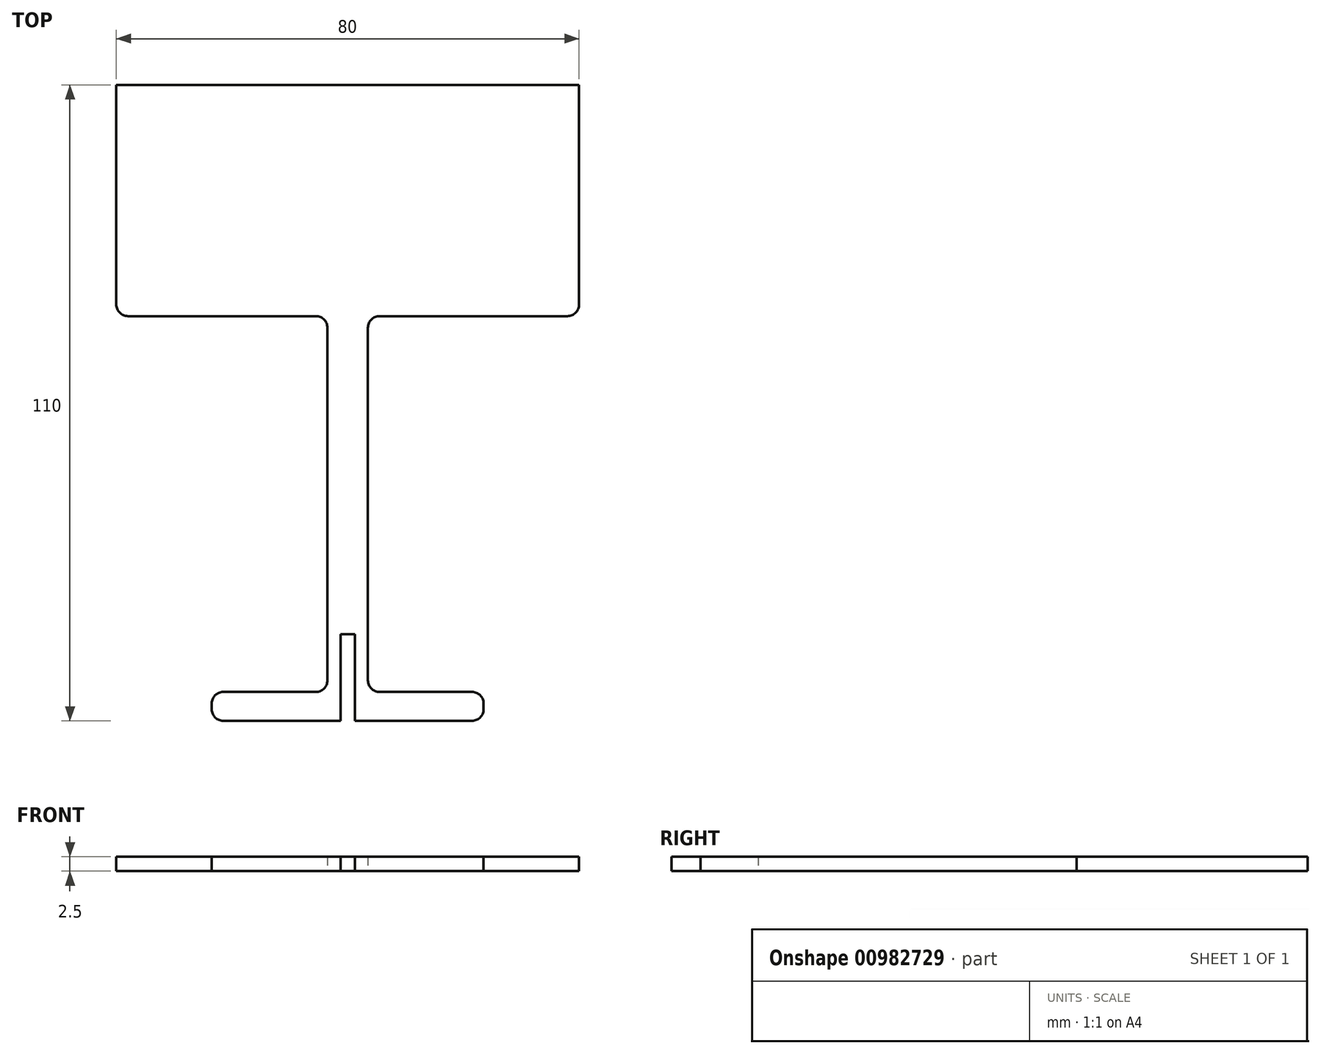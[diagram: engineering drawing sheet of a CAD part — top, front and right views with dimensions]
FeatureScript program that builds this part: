
annotation { "Feature Type Name" : "Feature", "Feature Type Description" : "" }
export const myFeature = defineFeature(function(context is Context, id is Id, definition is map)
    precondition{}
    {
        {
            var Q0;
            Q0=qCreatedBy(makeId("Top.planeOp"),FACE);
            var sketch = newSketch(context, id + "F0", { "sketchPlane" : qUnion([Q0])});
            skLineSegment(sketch, "E0", {"start": v(-40, 0) * mm, "end": v(40, 0) * mm});
            skPoint(sketch, "E1", {"position": v(0, 0) * mm});
            skLineSegment(sketch, "E2", {"start": v(-3.5, 0) * mm, "end": v(-3.5, -65) * mm});
            skLineSegment(sketch, "E3", {"start": v(-3.5, -65) * mm, "end": v(-23.5, -65) * mm});
            skLineSegment(sketch, "E4", {"start": v(-23.5, -65) * mm, "end": v(-23.5, -70) * mm});
            skLineSegment(sketch, "E5", {"start": v(-23.5, -70) * mm, "end": v(23.5, -70) * mm});
            skLineSegment(sketch, "E6", {"start": v(23.5, -70) * mm, "end": v(23.5, -65) * mm});
            skLineSegment(sketch, "E7", {"start": v(23.5, -65) * mm, "end": v(3.5, -65) * mm});
            skLineSegment(sketch, "E8", {"start": v(3.5, -65) * mm, "end": v(3.5, 0) * mm});
            skLineSegment(sketch, "E9.bottom", {"start": v(1.25, -70) * mm, "end": v(-1.25, -70) * mm});
            skLineSegment(sketch, "E9.top", {"start": v(1.25, -55) * mm, "end": v(-1.25, -55) * mm});
            skLineSegment(sketch, "E9.left", {"start": v(1.25, -70) * mm, "end": v(1.25, -55) * mm});
            skLineSegment(sketch, "E9.right", {"start": v(-1.25, -70) * mm, "end": v(-1.25, -55) * mm});
            skPoint(sketch, "E9.middle", {"position": v(0, -62.5) * mm});
            skLineSegment(sketch, "E10.bottom", {"start": v(-23.5, -70) * mm, "end": v(-17.5, -70) * mm});
            skLineSegment(sketch, "E10.top", {"start": v(-23.5, -70.3) * mm, "end": v(-17.5, -70.3) * mm});
            skLineSegment(sketch, "E10.left", {"start": v(-23.5, -70) * mm, "end": v(-23.5, -70.3) * mm});
            skLineSegment(sketch, "E10.right", {"start": v(-17.5, -70) * mm, "end": v(-17.5, -70.3) * mm});
            skLineSegment(sketch, "E11.MirrorCS", {"start": v(23.5, -70) * mm, "end": v(17.5, -70) * mm});
            skLineSegment(sketch, "E12.MirrorCS", {"start": v(17.5, -70) * mm, "end": v(17.5, -70.3) * mm});
            skLineSegment(sketch, "E13.MirrorCS", {"start": v(23.5, -70.3) * mm, "end": v(17.5, -70.3) * mm});
            skLineSegment(sketch, "E14.MirrorCS", {"start": v(23.5, -70) * mm, "end": v(23.5, -70.3) * mm});
            skLineSegment(sketch, "E15", {"start": v(-40, 0) * mm, "end": v(-40, 40) * mm});
            skLineSegment(sketch, "E16", {"start": v(-40, 40) * mm, "end": v(40, 40) * mm});
            skLineSegment(sketch, "E17", {"start": v(40, 40) * mm, "end": v(40, 0) * mm});
            skSolve(sketch);
        }
        {
            var Q0;
            {var subQ0=sQuery(id+"F0.wireOp",EDGE,"im0v1Rov-prSM-cwdN-f0IW-ScqFdnQkXUSi");Q0=makeQuery(id+"F0.imprint","IMPRINT",FACE,{"disambiguationData":[TD([[makeQuery(id+"F0.imprint","IMPRINT",EDGE,{"derivedFrom":subQ0}),1.0]])]});}
            var Q1;
            {var subQ7=sQuery(id+"F0.wireOp",EDGE,"E2");Q1=makeQuery(id+"F0.imprint","IMPRINT",FACE,{"disambiguationData":[TD([[makeQuery(id+"F0.imprint","IMPRINT",EDGE,{"derivedFrom":subQ7}),1.0]])]});}
            var Q2;
            Q2=makeQuery(id+"F0.imprint","IMPRINT",FACE,{"disambiguationData":[TD([[makeQuery(id+"F0.imprint","IMPRINT",EDGE,{"derivedFrom":sQuery(id+"F0.wireOp",EDGE,"E10.bottom")}),-1.0]])]});
            var Q3;
            Q3=makeQuery(id+"F0.imprint","IMPRINT",FACE,{"disambiguationData":[TD([[makeQuery(id+"F0.imprint","IMPRINT",EDGE,{"derivedFrom":sQuery(id+"F0.wireOp",EDGE,"E11.MirrorCS")}),1.0]])]});
            var Q4;
            {var subQ0=sQuery(id+"F0.wireOp",EDGE,"E15");Q4=makeQuery(id+"F0.imprint","IMPRINT",FACE,{"disambiguationData":[TD([[makeQuery(id+"F0.imprint","IMPRINT",EDGE,{"derivedFrom":subQ0}),-1.0]])]});}
            extrude(context, id + "F1", {"entities" : qUnion([Q0, Q1, Q2, Q3, Q4]), "flatOperationType" : FlatOperationType.REMOVE, "depth" : 2.5 * mm, "offsetDistance" : 25 * mm, "domain" : OperationDomain.MODEL});
        }
        {
            var Q0;
            Q0=makeQuery(id+"F1.opExtrude","SWEPT_EDGE",EDGE,{"disambiguationData":[OSD([sQuery(id+"F0.wireOp",EDGE,"E0"),sQuery(id+"F0.wireOp",EDGE,"E2")])]});
            var Q1;
            Q1=makeQuery(id+"F1.opExtrude","SWEPT_EDGE",EDGE,{"disambiguationData":[OSD([sQuery(id+"F0.wireOp",EDGE,"E0"),sQuery(id+"F0.wireOp",EDGE,"E8")])]});
            var Q2;
            Q2=makeQuery(id+"F1.opExtrude","SWEPT_EDGE",EDGE,{"disambiguationData":[OSD([sQuery(id+"F0.wireOp",EDGE,"E0"),sQuery(id+"F0.wireOp",EDGE,"im0v1Rov-prSM-cwdN-f0IW-ScqFdnQkXUSi")])]});
            var Q3;
            Q3=makeQuery(id+"F1.opExtrude","SWEPT_EDGE",EDGE,{"disambiguationData":[OSD([sQuery(id+"F0.wireOp",EDGE,"E0"),sQuery(id+"F0.wireOp",EDGE,"IfBi3EXo-PReU-dRJG-joro-0UU4bWJMkuGZ")])]});
            var Q4;
            Q4=makeQuery(id+"F1.opExtrude","SWEPT_EDGE",EDGE,{"disambiguationData":[OSD([sQuery(id+"F0.wireOp",EDGE,"im0v1Rov-prSM-cwdN-f0IW-ScqFdnQkXUSi"),sQuery(id+"F0.wireOp",EDGE,"IfBi3EXo-PReU-dRJG-joro-0UU4bWJMkuGZ")])]});
            var Q5;
            Q5=makeQuery(id+"F1.opExtrude","SWEPT_EDGE",EDGE,{"disambiguationData":[OSD([sQuery(id+"F0.wireOp",EDGE,"E7"),sQuery(id+"F0.wireOp",EDGE,"E8")])]});
            var Q6;
            Q6=makeQuery(id+"F1.opExtrude","SWEPT_EDGE",EDGE,{"disambiguationData":[OSD([sQuery(id+"F0.wireOp",EDGE,"E2"),sQuery(id+"F0.wireOp",EDGE,"E3")])]});
            var Q7;
            Q7=makeQuery(id+"F1.opExtrude","SWEPT_EDGE",EDGE,{"disambiguationData":[OSD([sQuery(id+"F0.wireOp",EDGE,"E3"),sQuery(id+"F0.wireOp",EDGE,"E4")])]});
            var Q8;
            Q8=makeQuery(id+"F1.opExtrude","SWEPT_EDGE",EDGE,{"disambiguationData":[OSD([sQuery(id+"F0.wireOp",EDGE,"E6"),sQuery(id+"F0.wireOp",EDGE,"E7")])]});
            var Q9;
            Q9=makeQuery(id+"F1.opExtrude","SWEPT_EDGE",EDGE,{"disambiguationData":[OSD([sQuery(id+"F0.wireOp",EDGE,"E10.top"),sQuery(id+"F0.wireOp",EDGE,"E10.left")])]});
            var Q10;
            Q10=makeQuery(id+"F1.opExtrude","SWEPT_EDGE",EDGE,{"disambiguationData":[OSD([sQuery(id+"F0.wireOp",EDGE,"E13.MirrorCS"),sQuery(id+"F0.wireOp",EDGE,"E14.MirrorCS")])]});
            fillet(context, id + "F2", {"entities" : qUnion([Q0, Q1, Q2, Q3, Q4, Q5, Q6, Q7, Q8, Q9, Q10]), "radius" : 2 * mm, "tangentPropagation" : true, "allowEdgeOverflow" : false});
        }
    });
